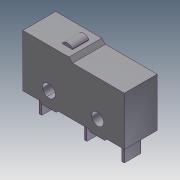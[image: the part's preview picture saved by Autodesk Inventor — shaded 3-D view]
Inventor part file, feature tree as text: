
AUTODESK INVENTOR PART (.ipt)
format: ipt  version: 2015 SP1 (Build 190203100, 203)  size: 162,304 bytes
history: native  units: in
note: dims shown in document units (in); Inventor stores cm internally (conversion verified against a paired STEP export)
features: other x2, sketch x2, imported_body x2
ambient origin geometry x8: Origin, YZ Plane, XZ Plane, XY Plane, X Axis, Y Axis, Z Axis, Center Point
bodies: Body1 (feature_tree)
feature tree (6):
  parser-record x1  (decoder bookkeeping rows leaked as tree rows — omitted from the tree; the rows remain in map.json)
  sketch  "Sketch1"  dims[d0=0.6102in]
  sketch  "Sketch2"
  other  "NONE_1"
  imported_body  "Base1"
  imported_body  "Base2"
